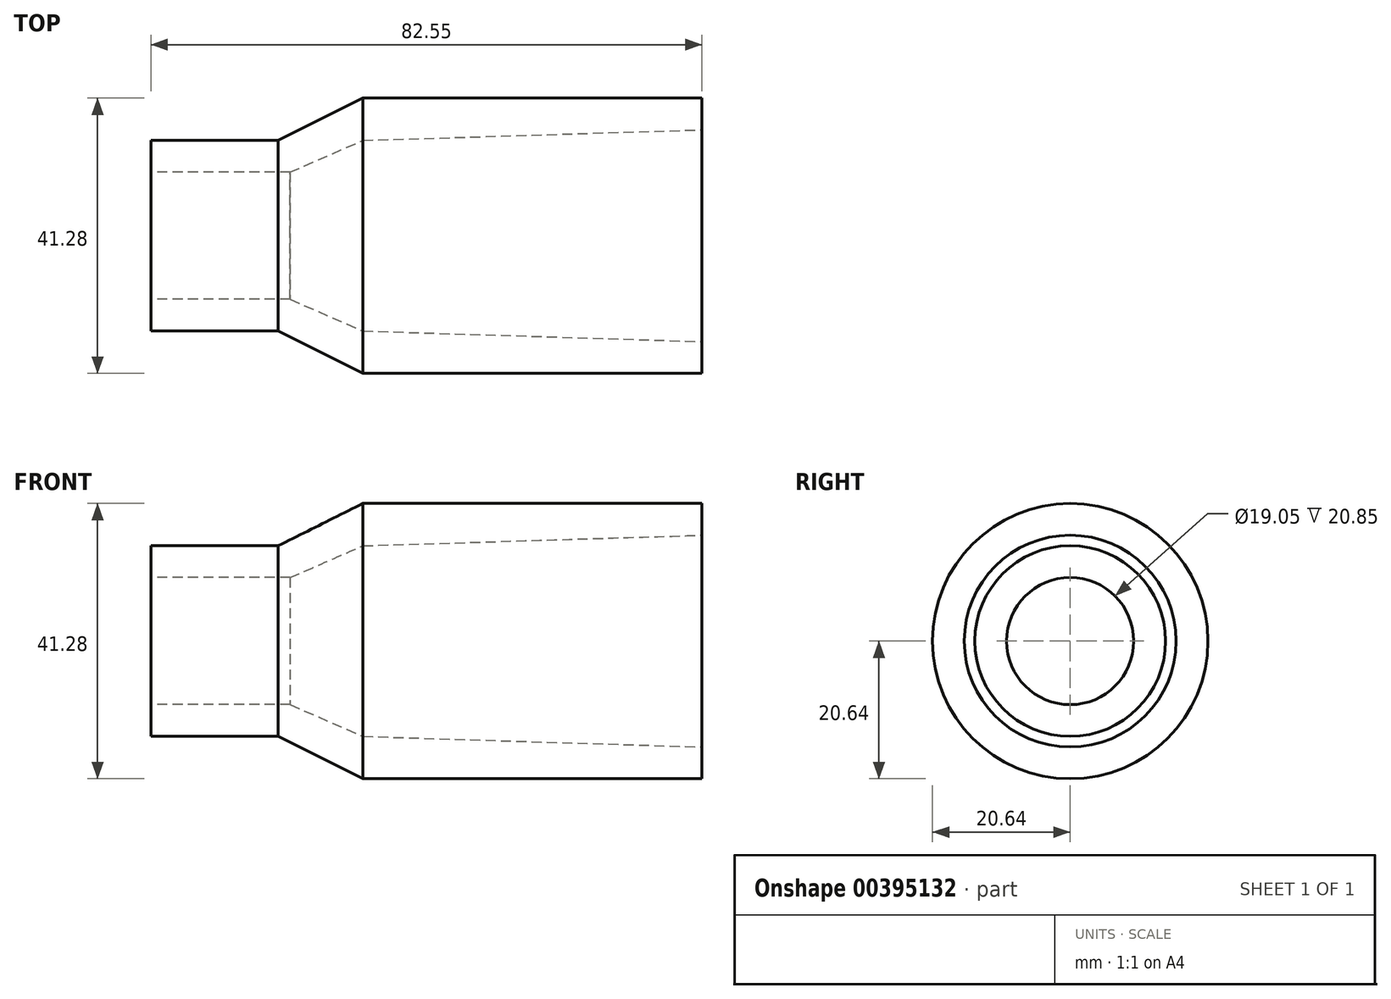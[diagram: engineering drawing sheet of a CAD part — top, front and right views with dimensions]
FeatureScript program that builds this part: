
annotation { "Feature Type Name" : "Feature", "Feature Type Description" : "" }
export const myFeature = defineFeature(function(context is Context, id is Id, definition is map)
    precondition{}
    {
        {
            var Q0;
            Q0=qCreatedBy(makeId("Front.planeOp"),FACE);
            var sketch = newSketch(context, id + "F0", { "sketchPlane" : qUnion([Q0])});
            skLineSegment(sketch, "E0", {"start": v(0, 14.29) * mm, "end": v(19.05, 14.29) * mm});
            skLineSegment(sketch, "E1", {"start": v(31.75, 20.64) * mm, "end": v(82.55, 20.64) * mm});
            skLineSegment(sketch, "E2", {"start": v(82.55, 20.64) * mm, "end": v(82.55, 15.88) * mm});
            skLineSegment(sketch, "E3", {"start": v(82.55, 15.88) * mm, "end": v(31.75, 14.29) * mm});
            skLineSegment(sketch, "E4", {"start": v(20.85, 9.53) * mm, "end": v(0, 9.53) * mm});
            skLineSegment(sketch, "E5", {"start": v(0, 9.52) * mm, "end": v(0, 14.29) * mm});
            skLineSegment(sketch, "E6", {"start": v(19.05, 14.29) * mm, "end": v(31.75, 20.64) * mm});
            skLineSegment(sketch, "E7", {"start": v(20.85, 9.52) * mm, "end": v(31.75, 14.29) * mm});
            skPoint(sketch, "E8", {"position": v(0, 0) * mm});
            skLineSegment(sketch, "E9", {"start": v(0, 0) * mm, "end": v(97.24, 0) * mm, "construction": true});
            skSolve(sketch);
        }
        {
            var Q0;
            Q0 = qSketchRegion(id + "F0", true);
            var Q1;
            Q1=sQuery(id+"F0.wireOp",EDGE,"E9");
            revolve(context, id + "F1", {"entities" : qUnion([Q0]), "axis" : qUnion([Q1]), "revolveType" : RevolveType.FULL});
        }
    });
